annotation { "Feature Type Name" : "Feature", "Feature Type Description" : "" }
export const myFeature = defineFeature(function(context is Context, id is Id, definition is map)
    precondition{}
    {
        {
            var Q0;
            Q0=qCreatedBy(makeId("Front.planeOp"),FACE);
            var sketch = newSketch(context, id + "F0", { "sketchPlane" : qUnion([Q0])});
            skLineSegment(sketch, "E0.bottom", {"start": v(-14.28, 27.25) * mm, "end": v(55.73, 27.25) * mm});
            skLineSegment(sketch, "E0.top", {"start": v(-14.28, -74.98) * mm, "end": v(55.73, -74.98) * mm});
            skLineSegment(sketch, "E0.left", {"start": v(-14.28, 27.25) * mm, "end": v(-14.28, -74.98) * mm});
            skLineSegment(sketch, "E0.right", {"start": v(55.73, 27.25) * mm, "end": v(55.73, -74.98) * mm});
            skSolve(sketch);
        }
        {
            var Q0;
            Q0=makeQuery(id+"F0.imprint","IMPRINT",FACE,{"disambiguationData":[TD([[makeQuery(id+"F0.imprint","IMPRINT",EDGE,{"derivedFrom":sQuery(id+"F0.wireOp",EDGE,"E0.bottom")}),-1.0]])]});
            extrude(context, id + "F1", {"entities" : qUnion([Q0]), "depth" : 25.4 * mm});
        }
        {
            var Q0;
            Q0=makeQuery(id+"F1.opExtrude","CAP_EDGE",EDGE,{"disambiguationData":[OSD([sQuery(id+"F0.wireOp",EDGE,"E0.bottom")])],"isStart":true});
            var Q1;
            Q1=makeQuery(id+"F1.opExtrude","SWEPT_EDGE",EDGE,{"disambiguationData":[OSD([sQuery(id+"F0.wireOp",EDGE,"E0.bottom"),sQuery(id+"F0.wireOp",EDGE,"E0.right")])]});
            var Q2;
            Q2=makeQuery(id+"F1.opExtrude","CAP_EDGE",EDGE,{"disambiguationData":[OSD([sQuery(id+"F0.wireOp",EDGE,"E0.bottom")])],"isStart":false});
            var Q3;
            Q3=makeQuery(id+"F1.opExtrude","SWEPT_EDGE",EDGE,{"disambiguationData":[OSD([sQuery(id+"F0.wireOp",EDGE,"E0.bottom"),sQuery(id+"F0.wireOp",EDGE,"E0.left")])]});
            var Q4;
            Q4=makeQuery(id+"F1.opExtrude","CAP_EDGE",EDGE,{"disambiguationData":[OSD([sQuery(id+"F0.wireOp",EDGE,"E0.right")])],"isStart":false});
            var Q5;
            Q5=makeQuery(id+"F1.opExtrude","CAP_EDGE",EDGE,{"disambiguationData":[OSD([sQuery(id+"F0.wireOp",EDGE,"E0.right")])],"isStart":true});
            var Q6;
            Q6=makeQuery(id+"F1.opExtrude","CAP_EDGE",EDGE,{"disambiguationData":[OSD([sQuery(id+"F0.wireOp",EDGE,"E0.left")])],"isStart":false});
            var Q7;
            Q7=makeQuery(id+"F1.opExtrude","CAP_EDGE",EDGE,{"disambiguationData":[OSD([sQuery(id+"F0.wireOp",EDGE,"E0.left")])],"isStart":true});
            fillet(context, id + "F2", {"entities" : qUnion([Q0, Q1, Q2, Q3, Q4, Q5, Q6, Q7]), "radius" : 5.08 * mm, "tangentPropagation" : true, "allowEdgeOverflow" : false});
        }
        {
            var Q0;
            Q0=makeQuery(id+"F1.opExtrude","CAP_FACE",FACE,{"disambiguationData":[OSD([sQuery(id+"F0.wireOp",EDGE,"E0.bottom"),sQuery(id+"F0.wireOp",EDGE,"E0.top"),sQuery(id+"F0.wireOp",EDGE,"E0.left"),sQuery(id+"F0.wireOp",EDGE,"E0.right")])],"isStart":false});
            var sketch = newSketch(context, id + "F3", { "sketchPlane" : qUnion([Q0])});
            skText(sketch, "E1", { "text": "Pioneer", "fontName": "OpenSans-Regular.ttf"});
            skText(sketch, "E2", { "text": "Seed Corn", "fontName": "OpenSans-Regular.ttf"});
            skText(sketch, "E3", { "text": "\"Science", "fontName": "OpenSans-Regular.ttf"});
            skText(sketch, "E4", { "text": "with service,", "fontName": "OpenSans-Regular.ttf"});
            skText(sketch, "E5", { "text": "Delivering", "fontName": "OpenSans-Regular.ttf"});
            skText(sketch, "E6", { "text": "success.\"", "fontName": "OpenSans-Regular.ttf"});
            skText(sketch, "E7", { "text": "Dupont", "fontName": "OpenSans-Regular.ttf"});
            const initialGuessF3  = {"E1": [-0.00672, -0.02672, 1, 0, 0.01063], "E2": [-0.006, -0.03462, 1, 0, 0.0079], "E3": [-0.0033, -0.05345, 1, 0, 0.00814], "E4": [-0.00469, -0.05986, 1, 0, 0.0064], "E5": [-0.00122, -0.06575, 1, 0, 0.00589], "E6": [0.00242, -0.07112, 1, 0, 0.00537], "E7": [-0.00711, -0.0458, 1, 0, 0.01118]};
            skSetInitialGuess(sketch, initialGuessF3);
            skSolve(sketch);
        }
        {
            var Q0;
            Q0 = qSketchRegion(id + "F3", true);
            extrude(context, id + "F4", {"entities" : qUnion([Q0]), "operationType" : NewBodyOperationType.ADD, "depth" : 3.05 * mm});
        }
        {
            var Q0;
            {var subQ0=sQuery(id+"F0.wireOp",EDGE,"E0.right");var subQ1=sQuery(id+"F0.wireOp",EDGE,"E0.left");var subQ2=sQuery(id+"F0.wireOp",EDGE,"E0.bottom");var subQ8=sQuery(id+"F0.wireOp",EDGE,"E0.top");Q0=makeQuery(id+"F4.boolean.opBoolean","SPLIT",FACE,{"disambiguationData":[TD([makeQuery(id+"F1.opExtrude","SWEPT_FACE",FACE,{"disambiguationData":[OSD([subQ8])]})])],"derivedFrom":makeQuery(id+"F1.opExtrude","CAP_FACE",FACE,{"disambiguationData":[OSD([subQ2,subQ8,subQ1,subQ0])],"isStart":false})});}
            var sketch = newSketch(context, id + "F5", { "sketchPlane" : qUnion([Q0])});
            skLineSegment(sketch, "E8", {"start": v(6.22, 15.2) * mm, "end": v(34.78, 15.2) * mm});
            skLineSegment(sketch, "E9", {"start": v(0.13, 10.67) * mm, "end": v(-4.86, -6.09) * mm});
            skLineSegment(sketch, "E10", {"start": v(40.72, 11.11) * mm, "end": v(47.08, -5.64) * mm});
            skLineSegment(sketch, "E11", {"start": v(1.23, -14.25) * mm, "end": v(41.14, -14.25) * mm});
            skPoint(sketch, "E12.visualSharp", {"position": v(1.48, 15.2) * mm});
            skArc(sketch, "E12.filletArc", {"start": v(6.22, 15.2) * mm, "mid": v(2.42, 13.95) * mm, "end": v(0.13, 10.67) * mm});
            skPoint(sketch, "E13.visualSharp", {"position": v(39.16, 15.2) * mm});
            skArc(sketch, "E13.filletArc", {"start": v(40.72, 11.11) * mm, "mid": v(38.39, 14.08) * mm, "end": v(34.78, 15.2) * mm});
            skPoint(sketch, "E14.visualSharp", {"position": v(50.34, -14.25) * mm});
            skArc(sketch, "E14.filletArc", {"start": v(41.14, -14.25) * mm, "mid": v(46.37, -11.5) * mm, "end": v(47.08, -5.64) * mm});
            skPoint(sketch, "E15.visualSharp", {"position": v(-7.29, -14.25) * mm});
            skArc(sketch, "E15.filletArc", {"start": v(-4.86, -6.09) * mm, "mid": v(-3.86, -11.7) * mm, "end": v(1.23, -14.25) * mm});
            skArc(sketch, "E16.0", {"start": v(6.22, 13.01) * mm, "mid": v(3.74, 12.19) * mm, "end": v(2.24, 10.04) * mm});
            skLineSegment(sketch, "E16.1", {"start": v(2.24, 10.04) * mm, "end": v(-2.75, -6.71) * mm});
            skLineSegment(sketch, "E16.2", {"start": v(6.22, 13.01) * mm, "end": v(34.78, 13.01) * mm});
            skArc(sketch, "E16.3", {"start": v(-2.75, -6.71) * mm, "mid": v(-2.1, -10.38) * mm, "end": v(1.23, -12.05) * mm});
            skArc(sketch, "E16.4", {"start": v(38.66, 10.33) * mm, "mid": v(37.14, 12.28) * mm, "end": v(34.78, 13.01) * mm});
            skLineSegment(sketch, "E16.5", {"start": v(38.66, 10.33) * mm, "end": v(45.02, -6.42) * mm});
            skArc(sketch, "E16.6", {"start": v(41.14, -12.05) * mm, "mid": v(44.56, -10.26) * mm, "end": v(45.02, -6.42) * mm});
            skLineSegment(sketch, "E16.7", {"start": v(1.23, -12.05) * mm, "end": v(41.14, -12.05) * mm});
            skEllipticalArc(sketch, "E17", {});
            skLineSegment(sketch, "E18.0", {"start": v(-15.55, -81.33) * mm, "end": v(57, -81.33) * mm});
            skLineSegment(sketch, "E18.1", {"start": v(-15.55, 28.52) * mm, "end": v(-15.55, -81.33) * mm});
            skLineSegment(sketch, "E18.2", {"start": v(57, 28.52) * mm, "end": v(-15.55, 28.52) * mm});
            skLineSegment(sketch, "E18.3", {"start": v(57, -81.33) * mm, "end": v(57, 28.52) * mm});
            skPoint(sketch, "E19.endSnap0", {"position": v(21.18, -12.05) * mm});
            skArc(sketch, "E20", {"start": v(18.72, -1.5) * mm, "mid": v(14.34, 3.38) * mm, "end": v(7.87, 4.36) * mm});
            skArc(sketch, "E21", {"start": v(18.9, 4.36) * mm, "mid": v(13.38, 6.8) * mm, "end": v(7.87, 4.36) * mm});
            skArc(sketch, "E22", {"start": v(20.5, 10.19) * mm, "mid": v(18.9, 7.5) * mm, "end": v(18.9, 4.36) * mm});
            skArc(sketch, "E23.MirrorCS", {"start": v(20.5, 10.19) * mm, "mid": v(22.1, 7.5) * mm, "end": v(22.1, 4.36) * mm});
            skArc(sketch, "E24.MirrorCS", {"start": v(22.28, -1.5) * mm, "mid": v(26.65, 3.38) * mm, "end": v(33.13, 4.36) * mm});
            skEllipticalArc(sketch, "E25.MirrorCS", {});
            skArc(sketch, "E26.MirrorCS", {"start": v(22.1, 4.36) * mm, "mid": v(27.61, 6.8) * mm, "end": v(33.13, 4.36) * mm});
            skFitSpline(sketch, "E27.0", {"points": [v(5.84, -4.4) * mm, v(5.8, -4.94) * mm, v(5.84, -5.46) * mm, v(6.05, -6.13) * mm, v(6.52, -6.88) * mm, v(7.34, -7.63) * mm, v(8.36, -8.24) * mm, v(9.54, -8.72) * mm, v(10.88, -9.07) * mm, v(12.3, -9.28) * mm, v(13.77, -9.35) * mm, v(15.25, -9.28) * mm, v(16.66, -9.07) * mm, v(18, -8.72) * mm, v(19.19, -8.24) * mm, v(20.2, -7.63) * mm, v(21.03, -6.88) * mm, v(21.5, -6.13) * mm, v(21.7, -5.46) * mm, v(21.75, -4.94) * mm, v(21.7, -4.4) * mm, v(21.5, -3.74) * mm, v(21.03, -3) * mm, v(20.2, -2.24) * mm, v(19.19, -1.63) * mm, v(18, -1.15) * mm, v(16.66, -0.8) * mm, v(15.25, -0.6) * mm, v(13.77, -0.52) * mm, v(12.3, -0.6) * mm, v(10.88, -0.8) * mm, v(9.54, -1.15) * mm, v(8.36, -1.63) * mm, v(7.34, -2.24) * mm, v(6.52, -3) * mm, v(6.05, -3.74) * mm, v(5.84, -4.4) * mm, v(5.8, -4.94) * mm, v(5.84, -5.46) * mm]});
            skFitSpline(sketch, "E27.1", {"points": [v(35.15, -5.46) * mm, v(35.2, -4.94) * mm, v(35.15, -4.4) * mm, v(34.95, -3.74) * mm, v(34.48, -3) * mm, v(33.66, -2.24) * mm, v(32.64, -1.63) * mm, v(31.45, -1.15) * mm, v(30.12, -0.8) * mm, v(28.7, -0.6) * mm, v(27.23, -0.52) * mm, v(25.75, -0.6) * mm, v(24.34, -0.8) * mm, v(23, -1.15) * mm, v(21.81, -1.63) * mm, v(20.8, -2.24) * mm, v(19.97, -3) * mm, v(19.5, -3.74) * mm, v(19.3, -4.4) * mm, v(19.25, -4.94) * mm, v(19.3, -5.46) * mm, v(19.5, -6.13) * mm, v(19.97, -6.88) * mm, v(20.8, -7.63) * mm, v(21.81, -8.24) * mm, v(23, -8.72) * mm, v(24.34, -9.07) * mm, v(25.75, -9.28) * mm, v(27.23, -9.35) * mm, v(28.7, -9.28) * mm, v(30.12, -9.07) * mm, v(31.45, -8.72) * mm, v(32.64, -8.24) * mm, v(33.66, -7.63) * mm, v(34.48, -6.88) * mm, v(34.95, -6.13) * mm, v(35.15, -5.46) * mm, v(35.2, -4.94) * mm, v(35.15, -4.4) * mm]});
            skPoint(sketch, "E28.endSnap0", {"position": v(20.5, -4.94) * mm});
            skLineSegment(sketch, "E29", {"start": v(20.5, -5.96) * mm, "end": v(20.5, -3.91) * mm});
            skArc(sketch, "E30", {"start": v(18.02, -7.7) * mm, "mid": v(20.01, -4.6) * mm, "end": v(17.42, -1.97) * mm});
            skArc(sketch, "E31.MirrorCS", {"start": v(22.98, -7.7) * mm, "mid": v(20.99, -4.6) * mm, "end": v(23.58, -1.97) * mm});
            const initialGuessF5  = {"E17": [0.013770982050797546, -0.004935326618921621, -1, 0, 0.007039807607890059, 0.003469664979679831, 3.4402612155722014, 2.8429240916073844], "E25.MirrorCS": [0.02722728015705317, -0.004935326618921621, 1, 0, 0.007039807607890059, 0.003469664979679831, 3.440261215572202, 2.842924091607385]};
            skSetInitialGuess(sketch, initialGuessF5);
            skSolve(sketch);
        }
        {
            var Q0;
            {var subQ0=sQuery(id+"F5.wireOp",EDGE,"E21");Q0=makeQuery(id+"F5.imprint","IMPRINT",FACE,{"disambiguationData":[TD([[makeQuery(id+"F5.imprint","IMPRINT",EDGE,{"derivedFrom":subQ0}),1.0]])]});}
            var Q1;
            {var subQ11=sQuery(id+"F5.wireOp",EDGE,"bcRaaHtF-7YMl-WAz6-eoUR-bihJ1Rc9SSvB");var subQ12=sQuery(id+"F5.wireOp",EDGE,"E17");var subQ16=makeQuery(id+"F5.imprint","INTERSECT",VERTEX,{"disambiguationData":[OD(0.0)],"derivedFrom":[subQ12,subQ11]});Q1=makeQuery(id+"F5.imprint","IMPRINT",FACE,{"disambiguationData":[TD([[makeQuery(id+"F5.imprint","IMPRINT",EDGE,{"disambiguationData":[TD([[subQ16,-1.0]])],"derivedFrom":subQ12}),-1.0]])]});}
            var Q2;
            Q2=makeQuery(id+"F5.imprint","IMPRINT",FACE,{"disambiguationData":[TD([[makeQuery(id+"F5.imprint","IMPRINT",EDGE,{"derivedFrom":sQuery(id+"F5.wireOp",EDGE,"E8")}),-1.0]])]});
            var Q3;
            {var subQ2=sQuery(id+"F5.wireOp",EDGE,"E17");var subQ5=makeQuery(id+"F5.imprint","INTERSECT",VERTEX,{"derivedFrom":[subQ2,sQuery(id+"F5.wireOp",EDGE,"kxWawhK6-ZoQB-UX04-u0J8-6Gt3aJMKLCZJ")]});Q3=makeQuery(id+"F5.imprint","IMPRINT",FACE,{"disambiguationData":[TD([[makeQuery(id+"F5.imprint","IMPRINT",EDGE,{"disambiguationData":[TD([[subQ5,-1.0]])],"derivedFrom":subQ2}),-1.0]])]});}
            var Q4;
            {var subQ6=sQuery(id+"F5.wireOp",EDGE,"E28");Q4=makeQuery(id+"F5.imprint","IMPRINT",FACE,{"disambiguationData":[TD([[makeQuery(id+"F5.imprint","IMPRINT",EDGE,{"derivedFrom":subQ6}),1.0]])]});}
            var Q5;
            {var subQ10=sQuery(id+"F5.wireOp",EDGE,"E30");var subQ11=sQuery(id+"F5.wireOp",EDGE,"E17");var subQ15=makeQuery(id+"F5.imprint","INTERSECT",VERTEX,{"disambiguationData":[OD(0.0)],"derivedFrom":[subQ11,subQ10]});Q5=makeQuery(id+"F5.imprint","IMPRINT",FACE,{"disambiguationData":[TD([[makeQuery(id+"F5.imprint","IMPRINT",EDGE,{"disambiguationData":[TD([[subQ15,1.0]])],"derivedFrom":subQ11}),-1.0]])]});}
            var Q6;
            {var subQ0=sQuery(id+"F5.wireOp",EDGE,"E29");Q6=makeQuery(id+"F5.imprint","IMPRINT",FACE,{"disambiguationData":[TD([[makeQuery(id+"F5.imprint","IMPRINT",EDGE,{"derivedFrom":subQ0}),1.0]])]});}
            var Q7;
            {var subQ0=sQuery(id+"F5.wireOp",EDGE,"E29");Q7=makeQuery(id+"F5.imprint","IMPRINT",FACE,{"disambiguationData":[TD([[makeQuery(id+"F5.imprint","IMPRINT",EDGE,{"derivedFrom":subQ0}),-1.0]])]});}
            extrude(context, id + "F6", {"entities" : qUnion([Q0, Q1, Q2, Q3, Q4, Q5, Q6, Q7]), "operationType" : NewBodyOperationType.ADD, "depth" : 3.05 * mm});
        }
    });